# Revit family: Seating-Casual-Naughtone-Construct_Table
name_source: partatom
category: Furniture
revit_build: Autodesk Revit 2014 (Build: 20130308_1515(x64)
units: mm (PartAtom-declared; Revit-internal decimal feet)

## types (1)
- Table
    AssetIdentifier = CON-TAB
    Barcode = 0
    COBie Description = Designed by Lee Walsh, The Construct stool and table range are wonderfully useful products that can be dropped into almost any situation. Construct has a fine balance of materials with a solid oak top and folded steel base that wears it's construction method on its sleeve.
    Cost = 0 $
    Current Revision = 1
    Depth = 600 mm
    Description = Table
    Height = 350 mm  [stored 1.14829 ft]
    Length = 600 mm
    Manufacturer = Naughtone
    Model = Construct
    Name = Furniture-Table-Casual-Naughtone-Construct_Table
    Product Code = CON-TAB
    Product URL = http://www.naughtone.com
    SerialNumber = 0
    TagNumber = 0
    Type Comments = Table
    TypeName = 600mmx600mmx350mm, Table
    URL = http://www.naughtone.com
    Uniclass = Pr_40_50_21_58
    WarrantyDuration = 60

note: [stored X ft] marks values corroborated as IEEE doubles in the binary element streams (Revit-internal decimal feet)

## geometry (parser evidence)
native form markers: Sweep x2
no freeform markers — native parametric forms only
